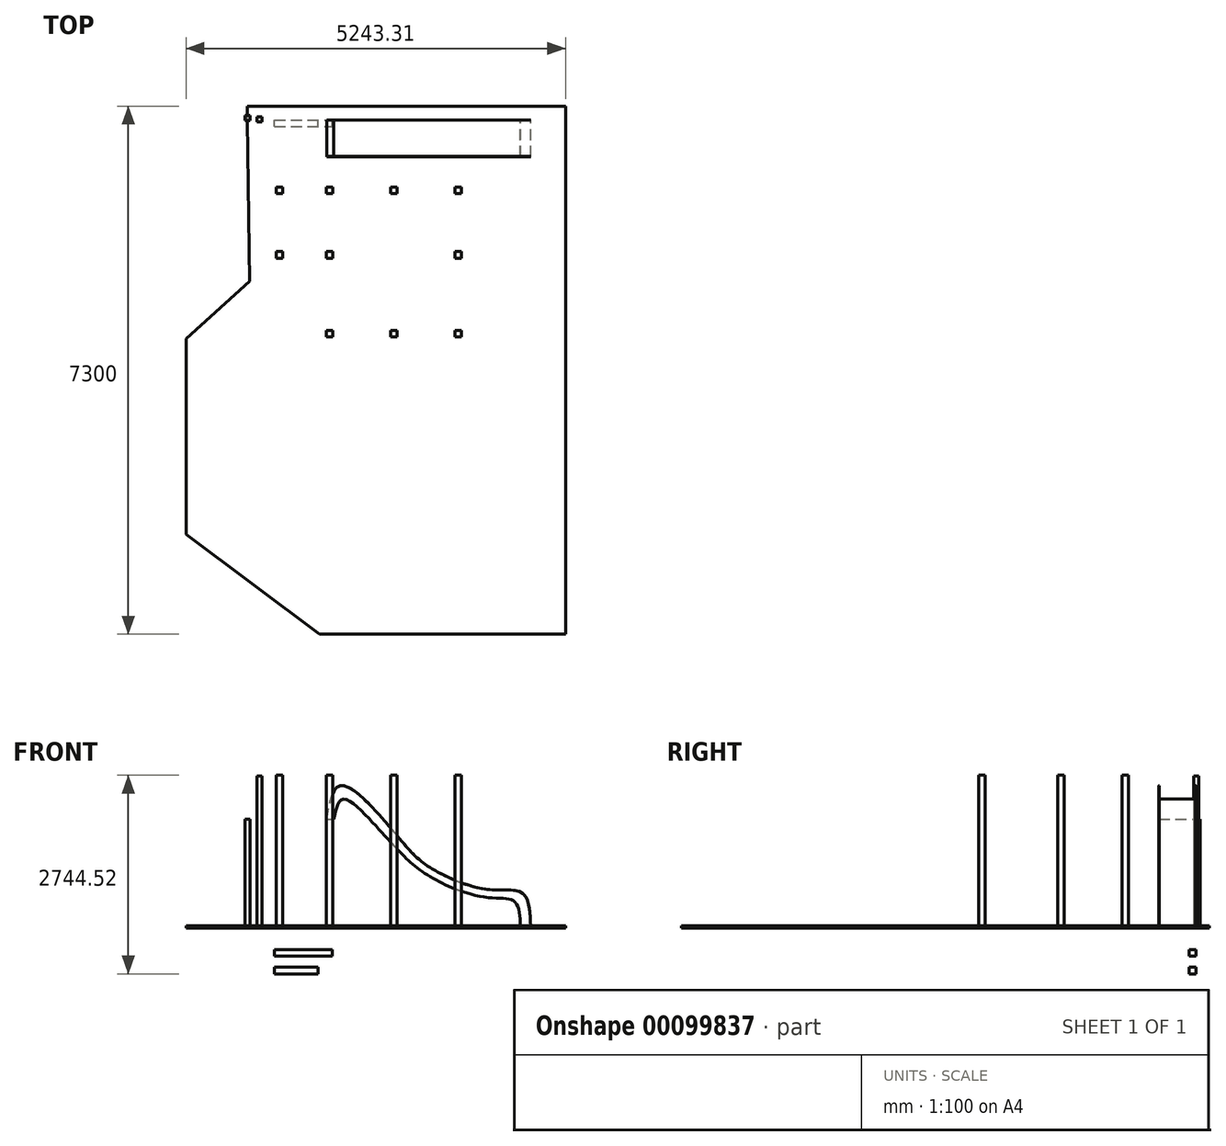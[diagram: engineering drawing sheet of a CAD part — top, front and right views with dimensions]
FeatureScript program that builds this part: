
annotation { "Feature Type Name" : "Feature", "Feature Type Description" : "" }
export const myFeature = defineFeature(function(context is Context, id is Id, definition is map)
    precondition{}
    {
        {
            var Q0;
            Q0=qCreatedBy(makeId("Top.planeOp"),FACE);
            var sketch = newSketch(context, id + "F0", { "sketchPlane" : qUnion([Q0])});
            skLineSegment(sketch, "E0.bottom", {"start": v(100, 41.37) * mm, "end": v(170, 41.37) * mm});
            skLineSegment(sketch, "E0.top", {"start": v(100, -28.63) * mm, "end": v(170, -28.63) * mm});
            skLineSegment(sketch, "E0.left", {"start": v(100, 41.37) * mm, "end": v(100, -28.63) * mm});
            skLineSegment(sketch, "E0.right", {"start": v(170, 41.37) * mm, "end": v(170, -28.63) * mm});
            skSolve(sketch);
        }
        {
            var Q0;
            Q0 = qSketchRegion(id + "F0", true);
            extrude(context, id + "F1", {"entities" : qUnion([Q0]), "depth" : 2100 * mm});
        }
        {
            var Q0;
            Q0=makeQuery(id+"F1.opExtrude","SWEPT_BODY",BODY,{"disambiguationData":[OSD([sQuery(id+"F0.wireOp",EDGE,"E0.bottom"),sQuery(id+"F0.wireOp",EDGE,"E0.top"),sQuery(id+"F0.wireOp",EDGE,"E0.left"),sQuery(id+"F0.wireOp",EDGE,"E0.right")])]});
            transform(context, id + "F2", {"entities" : qUnion([Q0]), "transformType" : TransformType.TRANSLATION_3D, "dx" : 100 * mm, "dy" : 0 * mm, "dz" : 0 * mm, "makeCopy" : true});
        }
        {
            var Q0;
            Q0=makeQuery(id+"F2.opPattern","COPY",BODY,{"derivedFrom":makeQuery(id+"F1.opExtrude","SWEPT_BODY",BODY,{"disambiguationData":[OSD([sQuery(id+"F0.wireOp",EDGE,"E0.bottom"),sQuery(id+"F0.wireOp",EDGE,"E0.top"),sQuery(id+"F0.wireOp",EDGE,"E0.left"),sQuery(id+"F0.wireOp",EDGE,"E0.right")])]}),"instanceName":"1"});
            deleteBodies(context, id + "F3", {"entities" : qUnion([Q0])});
        }
        {
            var Q0;
            Q0=qCreatedBy(makeId("Top.planeOp"),FACE);
            var sketch = newSketch(context, id + "F4", { "sketchPlane" : qUnion([Q0])});
            skLineSegment(sketch, "E1.bottom", {"start": v(-64.1, 59.45) * mm, "end": v(5.9, 59.45) * mm});
            skLineSegment(sketch, "E1.top", {"start": v(-64.1, -10.55) * mm, "end": v(5.9, -10.55) * mm});
            skLineSegment(sketch, "E1.left", {"start": v(-64.1, 59.45) * mm, "end": v(-64.1, -10.55) * mm});
            skLineSegment(sketch, "E1.right", {"start": v(5.9, 59.45) * mm, "end": v(5.9, -10.55) * mm});
            skSolve(sketch);
        }
        {
            var Q0;
            Q0=makeQuery(id+"F4.imprint","IMPRINT",FACE,{"disambiguationData":[TD([[makeQuery(id+"F4.imprint","IMPRINT",EDGE,{"derivedFrom":sQuery(id+"F4.wireOp",EDGE,"E1.bottom")}),-1.0]])]});
            extrude(context, id + "F5", {"entities" : qUnion([Q0]), "depth" : 1500 * mm});
        }
        {
            var Q0;
            Q0=qCreatedBy(makeId("Top.planeOp"),FACE);
            var sketch = newSketch(context, id + "F6", { "sketchPlane" : qUnion([Q0])});
            skLineSegment(sketch, "E2", {"start": v(-33.07, 189.6) * mm, "end": v(4366.93, 189.6) * mm});
            skLineSegment(sketch, "E3", {"start": v(4366.93, 189.6) * mm, "end": v(4366.93, -7110.4) * mm});
            skLineSegment(sketch, "E4", {"start": v(4366.93, -7110.4) * mm, "end": v(966.93, -7110.4) * mm});
            skLineSegment(sketch, "E5", {"start": v(966.93, -7110.4) * mm, "end": v(-876.38, -5729.47) * mm});
            skLineSegment(sketch, "E6", {"start": v(-876.38, -5729.47) * mm, "end": v(-876.38, -3023.86) * mm});
            skLineSegment(sketch, "E7", {"start": v(-876.38, -3023.86) * mm, "end": v(0, -2231.98) * mm});
            skLineSegment(sketch, "E8", {"start": v(0, -2231.98) * mm, "end": v(-33.07, 189.6) * mm});
            skSolve(sketch);
        }
        {
            var Q0;
            Q0=makeQuery(id+"F6.imprint","IMPRINT",FACE,{"disambiguationData":[TD([[makeQuery(id+"F6.imprint","IMPRINT",EDGE,{"derivedFrom":sQuery(id+"F6.wireOp",EDGE,"E2")}),-1.0]])]});
            extrude(context, id + "F7", {"entities" : qUnion([Q0]), "depth" : 30 * mm});
        }
        {
            var Q0;
            Q0=qCreatedBy(makeId("Front.planeOp"),FACE);
            var sketch = newSketch(context, id + "F8", { "sketchPlane" : qUnion([Q0])});
            skLineSegment(sketch, "E9", {"start": v(1064.17, 1500) * mm, "end": v(1164.17, 1500) * mm});
            skFitSpline(sketch, "E10", {"points": [v(1164.17, 1500) * mm, v(1196.62, 1636.4) * mm, v(1285.9, 1778.8) * mm, v(1660.3, 1500) * mm, v(1990.2, 1141.77) * mm, v(2466, 726.67) * mm, v(3304.87, 418.61) * mm, v(3669.8, 357) * mm, v(3740.89, 0) * mm], "startDerivative": vector(673.12, 3121.17) * mm, "endDerivative": vector(37.15, -3234.41) * mm});
            skFitSpline(sketch, "E11", {"points": [v(1064.17, 1500) * mm, v(1271.68, 1968.38) * mm, v(2072.63, 1233.78) * mm, v(2494.43, 835.68) * mm, v(3295.39, 532.36) * mm, v(3778.8, 475.48) * mm, v(3884.17, 0) * mm], "startDerivative": vector(788.33, 4694.52) * mm, "endDerivative": vector(159.84, -4135) * mm});
            skLineSegment(sketch, "E12", {"start": v(3884.17, 0) * mm, "end": v(3740.89, 0) * mm});
            skSolve(sketch);
        }
        {
            var Q0;
            Q0 = qSketchRegion(id + "F8", true);
            extrude(context, id + "F9", {"entities" : qUnion([Q0]), "depth" : 510 * mm});
        }
        {
            var Q0;
            Q0=makeQuery(id+"F9.opExtrude","SWEPT_FACE",FACE,{"disambiguationData":[OSD([sQuery(id+"F8.wireOp",EDGE,"E11")])]});
            shell(context, id + "F10", {"entities" : qUnion([Q0]), "thickness" : 2.5 * mm});
        }
        {
            var Q0;
            Q0=qCreatedBy(makeId("Top.planeOp"),FACE);
            var sketch = newSketch(context, id + "F11", { "sketchPlane" : qUnion([Q0])});
            skLineSegment(sketch, "E13.bottom", {"start": v(369.87, -931.15) * mm, "end": v(459.87, -931.15) * mm});
            skLineSegment(sketch, "E13.top", {"start": v(369.87, -1021.15) * mm, "end": v(459.87, -1021.15) * mm});
            skLineSegment(sketch, "E13.left", {"start": v(369.87, -931.15) * mm, "end": v(369.87, -1021.15) * mm});
            skLineSegment(sketch, "E13.right", {"start": v(459.87, -931.15) * mm, "end": v(459.87, -1021.15) * mm});
            skLineSegment(sketch, "E14.bottom", {"start": v(369.87, -1910.93) * mm, "end": v(459.87, -1910.93) * mm});
            skLineSegment(sketch, "E14.top", {"start": v(369.87, -1821.15) * mm, "end": v(459.87, -1821.15) * mm});
            skLineSegment(sketch, "E14.left", {"start": v(369.87, -1910.93) * mm, "end": v(369.87, -1821.15) * mm});
            skLineSegment(sketch, "E14.right", {"start": v(459.87, -1910.93) * mm, "end": v(459.87, -1821.15) * mm});
            skLineSegment(sketch, "E15.bottom", {"start": v(1059.87, -931.15) * mm, "end": v(1149.87, -931.15) * mm});
            skLineSegment(sketch, "E15.top", {"start": v(1059.87, -1021.15) * mm, "end": v(1149.87, -1021.15) * mm});
            skLineSegment(sketch, "E15.left", {"start": v(1059.87, -931.15) * mm, "end": v(1059.87, -1021.15) * mm});
            skLineSegment(sketch, "E15.right", {"start": v(1149.87, -931.15) * mm, "end": v(1149.87, -1021.15) * mm});
            skLineSegment(sketch, "E16.bottom", {"start": v(1059.87, -1821.15) * mm, "end": v(1149.87, -1821.15) * mm});
            skLineSegment(sketch, "E16.top", {"start": v(1059.87, -1910.93) * mm, "end": v(1149.87, -1910.93) * mm});
            skLineSegment(sketch, "E16.left", {"start": v(1059.87, -1821.15) * mm, "end": v(1059.87, -1910.93) * mm});
            skLineSegment(sketch, "E16.right", {"start": v(1149.87, -1821.15) * mm, "end": v(1149.87, -1910.93) * mm});
            skLineSegment(sketch, "E17.bottom", {"start": v(1059.87, -2910.93) * mm, "end": v(1149.87, -2910.93) * mm});
            skLineSegment(sketch, "E17.top", {"start": v(1059.87, -3000.93) * mm, "end": v(1149.87, -3000.93) * mm});
            skLineSegment(sketch, "E17.left", {"start": v(1059.87, -2910.93) * mm, "end": v(1059.87, -3000.93) * mm});
            skLineSegment(sketch, "E17.right", {"start": v(1149.87, -2910.93) * mm, "end": v(1149.87, -3000.93) * mm});
            skLineSegment(sketch, "E18.bottom", {"start": v(1949.87, -2910.93) * mm, "end": v(2039.87, -2910.93) * mm});
            skLineSegment(sketch, "E18.top", {"start": v(1949.87, -3000.93) * mm, "end": v(2039.87, -3000.93) * mm});
            skLineSegment(sketch, "E18.left", {"start": v(1949.87, -2910.93) * mm, "end": v(1949.87, -3000.93) * mm});
            skLineSegment(sketch, "E18.right", {"start": v(2039.87, -2910.93) * mm, "end": v(2039.87, -3000.93) * mm});
            skPoint(sketch, "E19.firstSnap0", {"position": v(1949.87, -2955.93) * mm});
            skLineSegment(sketch, "E19.bottom", {"start": v(1949.87, -931.15) * mm, "end": v(2039.87, -931.15) * mm});
            skLineSegment(sketch, "E19.top", {"start": v(1949.87, -1021.15) * mm, "end": v(2039.87, -1021.15) * mm});
            skLineSegment(sketch, "E19.left", {"start": v(1949.87, -931.15) * mm, "end": v(1949.87, -1021.15) * mm});
            skLineSegment(sketch, "E19.right", {"start": v(2039.87, -931.15) * mm, "end": v(2039.87, -1021.15) * mm});
            skLineSegment(sketch, "E20.bottom", {"start": v(2839.87, -931.15) * mm, "end": v(2929.87, -931.15) * mm});
            skLineSegment(sketch, "E20.top", {"start": v(2839.87, -1021.15) * mm, "end": v(2929.87, -1021.15) * mm});
            skLineSegment(sketch, "E20.left", {"start": v(2839.87, -931.15) * mm, "end": v(2839.87, -1021.15) * mm});
            skLineSegment(sketch, "E20.right", {"start": v(2929.87, -931.15) * mm, "end": v(2929.87, -1021.15) * mm});
            skPoint(sketch, "E21.oppositeSnap0", {"position": v(2929.87, -976.15) * mm});
            skLineSegment(sketch, "E22.bottom", {"start": v(2839.87, -2910.93) * mm, "end": v(2929.87, -2910.93) * mm});
            skLineSegment(sketch, "E22.top", {"start": v(2839.87, -3000.93) * mm, "end": v(2929.87, -3000.93) * mm});
            skLineSegment(sketch, "E22.left", {"start": v(2839.87, -2910.93) * mm, "end": v(2839.87, -3000.93) * mm});
            skLineSegment(sketch, "E22.right", {"start": v(2929.87, -2910.93) * mm, "end": v(2929.87, -3000.93) * mm});
            skLineSegment(sketch, "E23.bottom", {"start": v(2839.87, -1910.93) * mm, "end": v(2929.87, -1910.93) * mm});
            skLineSegment(sketch, "E23.top", {"start": v(2839.87, -1821.15) * mm, "end": v(2929.87, -1821.15) * mm});
            skLineSegment(sketch, "E23.left", {"start": v(2839.87, -1910.93) * mm, "end": v(2839.87, -1821.15) * mm});
            skLineSegment(sketch, "E23.right", {"start": v(2929.87, -1910.93) * mm, "end": v(2929.87, -1821.15) * mm});
            skSolve(sketch);
        }
        {
            var Q0;
            Q0 = qSketchRegion(id + "F11", true);
            extrude(context, id + "F12", {"entities" : qUnion([Q0]), "depth" : 2110 * mm});
        }
        {
            var Q0;
            Q0=qCreatedBy(makeId("Front.planeOp"),FACE);
            var sketch = newSketch(context, id + "F13", { "sketchPlane" : qUnion([Q0])});
            skLineSegment(sketch, "E24.bottom", {"start": v(343.15, -297.93) * mm, "end": v(1143.15, -297.93) * mm});
            skLineSegment(sketch, "E24.top", {"start": v(343.15, -387.93) * mm, "end": v(1143.15, -387.93) * mm});
            skLineSegment(sketch, "E24.left", {"start": v(343.15, -297.93) * mm, "end": v(343.15, -387.93) * mm});
            skLineSegment(sketch, "E24.right", {"start": v(1143.15, -297.93) * mm, "end": v(1143.15, -387.93) * mm});
            skLineSegment(sketch, "E25.bottom", {"start": v(343.15, -544.52) * mm, "end": v(943.15, -544.52) * mm});
            skLineSegment(sketch, "E25.top", {"start": v(343.15, -634.52) * mm, "end": v(943.15, -634.52) * mm});
            skLineSegment(sketch, "E25.left", {"start": v(343.15, -544.52) * mm, "end": v(343.15, -634.52) * mm});
            skLineSegment(sketch, "E25.right", {"start": v(943.15, -544.52) * mm, "end": v(943.15, -634.52) * mm});
            skSolve(sketch);
        }
        {
            var Q0;
            Q0 = qSketchRegion(id + "F13", true);
            extrude(context, id + "F14", {"entities" : qUnion([Q0]), "depth" : 90 * mm});
        }
    });
